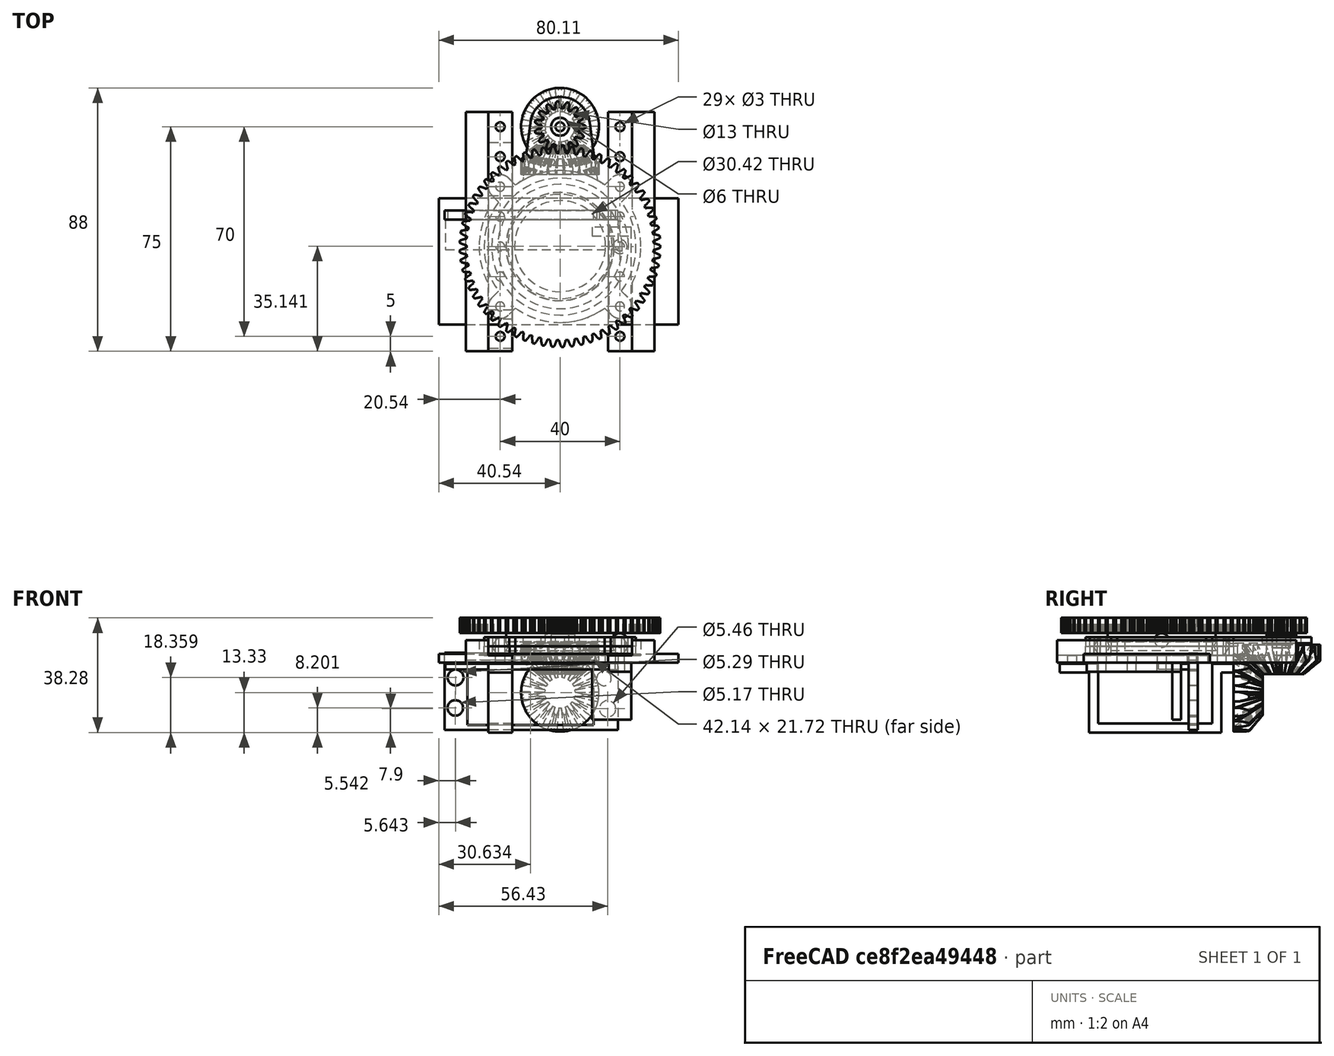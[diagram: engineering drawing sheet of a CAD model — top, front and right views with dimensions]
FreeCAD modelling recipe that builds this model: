
FCSTD DOCUMENT  (FreeCAD 0.16RUnknown)
Label: FrontTurntable2
License: CreativeCommons Attribution-NonCommercial
LicenseURL: http://creativecommons.org/licenses/by-nc/4.0/
objects: Sketcher::SketchObject×15, PartDesign::Pad×12, Part::Cylinder×5, Part::FeaturePython×4, Part::Feature×3, Part::MultiFuse×3, Part::Cut×3, Mesh::Feature×2, PartDesign::Revolution×2, Part::MultiCommon×1, Part::Sphere×1, Part::Mirroring×1
note: 64 computed .brp shape members not serialized (recipe doc carries the construction recipe); baked Part::Feature solids carry a one-line shape summary decoded from their .brp

FEATURE [Mesh::Feature] ParallaxServo
  Placement = pos=(-9.85,-60,0) rot=(-1,0,0;1.5708rad)
FEATURE [Part::FeaturePython] BevelGear  # WARN: FeaturePython — macro-defined, semantics opaque (R4)
  Placement = pos=(0,0,0) rot=(1,0,0;1.5708rad)
  backlash = 0
  clearance = 0.1
  height = 10
  m = 1.5
  numpoints = 6
  pitch_angle = 45
  pressure_angle = 20
  teeth = 15
FEATURE [Part::Cylinder] Cylinder
  Angle = 360
  Height = 10
  Placement = pos=(0,-6,0) rot=(1,0,0;1.5708rad)
  Radius = 13
FEATURE [Part::MultiCommon] Common
  Shapes = -> [BevelGear,Cylinder]
FEATURE [Part::Feature] Common001  label="Common"
  Placement = pos=(0,0,0) rot=(-1,0,0;1.5708rad)
  shape: bbox 39.21 x 39 x 10 mm, 93 faces (baked)
FEATURE [Sketcher::SketchObject] Sketch003
  Placement = pos=(0,-40,14) rot=(0.57735,0.57735,0.57735;2.0944rad)
  sketch-geometry (9):
    g0: LineSegment StartX=0 StartY=0 StartZ=0 EndX=18.1065 EndY=0 EndZ=0
    g1: LineSegment StartX=18.1065 StartY=3 StartZ=0 EndX=0 EndY=3 EndZ=0
    g2: LineSegment StartX=0 StartY=3 StartZ=0 EndX=0 EndY=0 EndZ=0
    g3: Circle [constr] CenterX=20 CenterY=1.5 CenterZ=0 NormalX=0 NormalY=0 NormalZ=1 Radius=2.25
    g4: LineSegment [constr] StartX=20 StartY=1.5 StartZ=0 EndX=0 EndY=1.5 EndZ=0
    g5: LineSegment StartX=18.1065 StartY=3 StartZ=0 EndX=17.4071 EndY=1.5 EndZ=0
    g6: LineSegment StartX=17.4071 StartY=1.5 StartZ=0 EndX=18.1065 EndY=0 EndZ=0
    g7: LineSegment [constr] StartX=18.1065 StartY=3 StartZ=0 EndX=18.1065 EndY=0 EndZ=0
    g8: Circle [constr] CenterX=20 CenterY=1.5 CenterZ=0 NormalX=0 NormalY=0 NormalZ=1 Radius=2.35
  constraints (23):
    c: Coincident(g-1,g0)
    c: PointOnObject(g1,g-2)
    c: Coincident(g1,g2)
    c: Coincident(g2,g0)
    c: PointOnObject(g0,g-1)
    c: Horizontal(g1)
    c: Radius(g3) = 2.25
    c: PointOnObject(g4,g2)
    c: Symmetric(g1,g-1,g4)
    c: DistanceY(g2,g2) = 3
    c: Coincident(g4,g3)
    c: Coincident(g5,g1)
    c: PointOnObject(g5,g4)
    c: Coincident(g6,g5)
    c: Coincident(g6,g0)
    c: Coincident(g7,g1)
    c: Coincident(g7,g0)
    c: Vertical(g7)
    c: Angle(g6,g5) = 2.26893
    c: Coincident(g8,g3)
    c: Radius(g8) = 2.35
    c: Tangent(g8,g5)
    c: DistanceX(g-1,g3) = 20
FEATURE [PartDesign::Revolution] Revolution
  Angle = 360
  Axis = (0,0,1)
  Base = (0,-40,14)
  Placement = pos=(0,-40,14) rot=(0.57735,0.57735,0.57735;2.0944rad)
  ReferenceAxis = -> Sketch003 [V_Axis]
  Reversed = true
  Sketch = -> Sketch003
FEATURE [Sketcher::SketchObject] Sketch004
  Placement = pos=(0,0,16) rot=(0.57735,0.57735,0.57735;2.0944rad)
  sketch-geometry (5):
    g0: Circle [constr] CenterX=20 CenterY=1.5 CenterZ=0 NormalX=0 NormalY=0 NormalZ=1 Radius=2.35
    g1: LineSegment StartX=20.7682 StartY=-1.5 StartZ=0 EndX=22.8688 EndY=1.5 EndZ=0
    g2: LineSegment StartX=22.8688 StartY=1.5 StartZ=0 EndX=25.3688 EndY=1.5 EndZ=0
    g3: LineSegment StartX=20.7682 StartY=-1.5 StartZ=0 EndX=25.3688 EndY=-1.5 EndZ=0
    g4: LineSegment StartX=25.3688 StartY=-1.5 StartZ=0 EndX=25.3688 EndY=1.5 EndZ=0
  constraints (15):
    c: Radius(g0) = 2.35
    c: DistanceX(g0) = 20
    c: DistanceY(g0) = 1.5
    c: Coincident(g1,g2)
    c: Horizontal(g2)
    c: Horizontal(g3)
    c: Coincident(g3,g4)
    c: Coincident(g4,g2)
    c: Vertical(g4)
    c: DistanceY(g-1,g2) = 1.5
    c: Tangent(g0,g1)
    c: DistanceX(g2,g2) = 2.5
    c: Coincident(g1,g3)
    c: Angle(g3,g1) = 0.959931
    c: DistanceY(g4,g4) = 3
FEATURE [PartDesign::Revolution] Revolution001
  Angle = 360
  Axis = (0,0,1)
  Base = (0,0,16)
  Placement = pos=(0,0,16) rot=(0.57735,0.57735,0.57735;2.0944rad)
  ReferenceAxis = -> Sketch004 [V_Axis]
  Reversed = true
  Sketch = -> Sketch004
FEATURE [Part::Sphere] Sphere
  Angle1 = -90
  Angle2 = 90
  Angle3 = 360
  Placement = pos=(20,-40,17.5) rot=(0,0,1;0rad)
  Radius = 2.35
FEATURE [Sketcher::SketchObject] Sketch005
  Placement = pos=(0,0,14.5) rot=(0,0,1;0rad)
  sketch-geometry (6):
    g0: Circle CenterX=20 CenterY=20 CenterZ=0 NormalX=0 NormalY=0 NormalZ=1 Radius=1.5
    g1: ArcOfCircle CenterX=0 CenterY=0 CenterZ=0 NormalX=0 NormalY=0 NormalZ=1 Radius=25 StartAngle=0.625164 EndAngle=0.945315
    g2: LineSegment [constr] StartX=20 StartY=20 StartZ=0 EndX=0 EndY=0 EndZ=0
    g3: ArcOfCircle CenterX=20 CenterY=20 CenterZ=0 NormalX=0 NormalY=0 NormalZ=1 Radius=4 StartAngle=5.42273 EndAngle=8.73713
    g4: LineSegment StartX=14.6372 StartY=20.267 StartZ=0 EndX=16.909 EndY=22.5389 EndZ=0
    g5: LineSegment StartX=20.2717 StartY=14.6308 StartZ=0 EndX=22.6084 EndY=16.9674 EndZ=0
  constraints (15):
    c: Radius(g0) = 1.5
    c: Coincident(g1,g-1)
    c: Radius(g1) = 25
    c: Coincident(g2,g0)
    c: Coincident(g2,g-1)
    c: Angle(g-1,g2) = 0.785398
    c: DistanceX(g-1,g0) = 20
    c: Coincident(g3,g0)
    c: Coincident(g4,g1)
    c: Coincident(g4,g3)
    c: Coincident(g5,g1)
    c: Coincident(g5,g3)
    c: Parallel(g5,g4)
    c: Parallel(g4,g2)
    c: Radius(g3) = 4
FEATURE [PartDesign::Pad] Pad  label="MountingJoint"
  Length = 3
  Length2 = 100
  Placement = pos=(0,0,14.5) rot=(0,0,1;0rad)
  Sketch = -> Sketch005
  Type = 0
FEATURE [Part::FeaturePython] Array  # Draft array (typed FeaturePython)
  Angle = 360
  ArrayType = 1
  Axis = (0,0,1)
  Base = -> Pad
  Center = (0,0,1)
  Fuse = false
  IntervalAxis = (0,0,0)
  IntervalX = (1,0,0)
  IntervalY = (0,1,0)
  IntervalZ = (0,0,0)
  NumberPolar = 4
  NumberX = 1
  NumberY = 1
  NumberZ = 1
FEATURE [Part::MultiFuse] Fusion
  Placement = pos=(0,-40,-2) rot=(0,0,1;0rad)
  Shapes = -> [Array,Revolution001]
FEATURE [Part::Feature] Fusion001  label="Fusion"
  Placement = pos=(0,-40,35) rot=(1,0,0;3.14159rad)
  shape: bbox 50.74 x 50.74 x 3 mm, 23 faces (baked)
FEATURE [Part::FeaturePython] InvoluteGear  # WARN: FeaturePython — macro-defined, semantics opaque (R4)
  Placement = pos=(0,0,20) rot=(0,0,1;0rad)
  backlash = 0
  beta = 0
  clearance = 0.25
  height = 5
  module = 1
  numpoints = 6
  pressure_angle = 20
  shift = 0
  simple = false
  teeth = 15
  undercut = false
FEATURE [Part::FeaturePython] InvoluteGear001  # WARN: FeaturePython — macro-defined, semantics opaque (R4)
  Placement = pos=(0,-40,20) rot=(0,0,1;0rad)
  backlash = 0
  beta = 0
  clearance = 0.25
  height = 5
  module = 1
  numpoints = 6
  pressure_angle = 20
  shift = 0
  simple = false
  teeth = 65
  undercut = false
FEATURE [Part::Cylinder] Cylinder001  label="Cylinder"
  Angle = 360
  Height = 10
  Placement = pos=(0,0,15) rot=(0,0,1;0rad)
  Radius = 3
FEATURE [Part::Cylinder] Cylinder002  label="Cylinder"
  Angle = 360
  Height = 3
  Placement = pos=(0,-40,17) rot=(0,0,1;0rad)
  Radius = 18
FEATURE [Sketcher::SketchObject] Sketch
  Placement = pos=(0,0,16.5) rot=(0,0,1;0rad)
  sketch-geometry (2):
    g0: Circle CenterX=0 CenterY=0 CenterZ=0 NormalX=0 NormalY=0 NormalZ=1 Radius=3
    g1: Circle CenterX=0 CenterY=0 CenterZ=0 NormalX=0 NormalY=0 NormalZ=1 Radius=5
  constraints (4):
    c: Coincident(g0,g-1)
    c: Radius(g0) = 3
    c: Coincident(g1,g-1)
    c: Radius(g1) = 5
FEATURE [PartDesign::Pad] Pad001  label="Bearing"
  Length = 3
  Length2 = 100
  Placement = pos=(0,0,16.5) rot=(0,0,1;0rad)
  Sketch = -> Sketch
  Type = 0
FEATURE [Part::Cylinder] Cylinder003  label="screw cutout"
  Angle = 360
  Height = 30
  Radius = 1.5
FEATURE [Part::Cylinder] Cylinder004  label="screw cutout"
  Angle = 360
  Height = 30
  Radius = 1.5
FEATURE [Part::Cut] Cut
  Base = -> Cylinder001
  Tool = -> Cylinder003
FEATURE [Part::Cut] Cut001
  Base = -> Common001
  Tool = -> Cylinder004
FEATURE [Sketcher::SketchObject] Sketch006
  Placement = pos=(0,0,10) rot=(0,0,1;0rad)
  sketch-geometry (5):
    g0: LineSegment StartX=-40.541 StartY=-66.0062 StartZ=0 EndX=39.5748 EndY=-66.0062 EndZ=0
    g1: LineSegment StartX=39.5748 StartY=-66.0062 StartZ=0 EndX=39.5748 EndY=-23.8558 EndZ=0
    g2: LineSegment StartX=39.5748 StartY=-23.8558 StartZ=0 EndX=-40.541 EndY=-23.8558 EndZ=0
    g3: LineSegment StartX=-40.541 StartY=-23.8558 StartZ=0 EndX=-40.541 EndY=-66.0062 EndZ=0
    g4: Circle CenterX=0 CenterY=-39.8595 CenterZ=0 NormalX=0 NormalY=0 NormalZ=1 Radius=15.2103
  constraints (9):
    c: Coincident(g0,g1)
    c: Coincident(g1,g2)
    c: Coincident(g2,g3)
    c: Coincident(g3,g0)
    c: Horizontal(g0)
    c: Horizontal(g2)
    c: Vertical(g1)
    c: Vertical(g3)
    c: PointOnObject(g4,g-2)
FEATURE [PartDesign::Pad] Pad002
  Length = 3
  Length2 = 100
  Placement = pos=(0,0,10) rot=(0,0,1;0rad)
  Sketch = -> Sketch006
  Type = 0
FEATURE [Sketcher::SketchObject] Sketch007
  Placement = pos=(0,-31,0) rot=(-1,0,0;4.71239rad)
  sketch-geometry (12):
    g0: LineSegment StartX=-38.5174 StartY=13.3252 StartZ=0 EndX=19.309 EndY=13.3252 EndZ=0
    g1: LineSegment StartX=19.309 StartY=13.3252 StartZ=0 EndX=19.309 EndY=-12.4201 EndZ=0
    g2: LineSegment StartX=19.309 StartY=-12.4201 StartZ=0 EndX=-38.5174 EndY=-12.4201 EndZ=0
    g3: LineSegment StartX=-38.5174 StartY=-12.4201 StartZ=0 EndX=-38.5174 EndY=13.3252 EndZ=0
    g4: LineSegment StartX=-30.9749 StartY=10.9116 StartZ=0 EndX=11.163 EndY=10.9116 EndZ=0
    g5: LineSegment StartX=11.163 StartY=10.9116 StartZ=0 EndX=11.163 EndY=-10.811 EndZ=0
    g6: LineSegment StartX=11.163 StartY=-10.811 StartZ=0 EndX=-30.9749 EndY=-10.811 EndZ=0
    g7: LineSegment StartX=-30.9749 StartY=-10.811 StartZ=0 EndX=-30.9749 EndY=10.9116 EndZ=0
    g8: Circle CenterX=14.6829 CenterY=4.77697 CenterZ=0 NormalX=0 NormalY=0 NormalZ=1 Radius=2.43241
    g9: Circle CenterX=15.8897 CenterY=-5.38037 CenterZ=0 NormalX=0 NormalY=0 NormalZ=1 Radius=2.73204
    g10: Circle CenterX=-34.897 CenterY=5.07867 CenterZ=0 NormalX=0 NormalY=0 NormalZ=1 Radius=2.64553
    g11: Circle CenterX=-34.9976 CenterY=-5.07867 CenterZ=0 NormalX=0 NormalY=0 NormalZ=1 Radius=2.58559
  constraints (16):
    c: Coincident(g0,g1)
    c: Coincident(g1,g2)
    c: Coincident(g2,g3)
    c: Coincident(g3,g0)
    c: Horizontal(g0)
    c: Horizontal(g2)
    c: Vertical(g1)
    c: Vertical(g3)
    c: Coincident(g4,g5)
    c: Coincident(g5,g6)
    c: Coincident(g6,g7)
    c: Coincident(g7,g4)
    c: Horizontal(g4)
    c: Horizontal(g6)
    c: Vertical(g5)
    c: Vertical(g7)
FEATURE [PartDesign::Pad] Pad003
  Length = 3
  Length2 = 100
  Placement = pos=(0,-31,0) rot=(-1,0,0;4.71239rad)
  Reversed = true
  Sketch = -> Sketch007
  Type = 0
FEATURE [Sketcher::SketchObject] Sketch008
  Placement = pos=(0,-31,0) rot=(1,0,0;1.5708rad)
  sketch-geometry (4):
    g0: LineSegment StartX=-38.2971 StartY=7.70587 StartZ=0 EndX=19.3119 EndY=7.70587 EndZ=0
    g1: LineSegment StartX=19.3119 StartY=7.70587 StartZ=0 EndX=19.3119 EndY=9.70587 EndZ=0
    g2: LineSegment StartX=19.3119 StartY=9.70587 StartZ=0 EndX=-38.2971 EndY=9.70587 EndZ=0
    g3: LineSegment StartX=-38.2971 StartY=9.70587 StartZ=0 EndX=-38.2971 EndY=7.70587 EndZ=0
  constraints (9):
    c: Coincident(g0,g1)
    c: Coincident(g1,g2)
    c: Coincident(g2,g3)
    c: Coincident(g3,g0)
    c: Horizontal(g0)
    c: Horizontal(g2)
    c: Vertical(g1)
    c: Vertical(g3)
    c: DistanceY(g1,g1) = 2
FEATURE [PartDesign::Pad] Pad004
  Length = 10
  Length2 = 100
  Placement = pos=(0,-31,0) rot=(1,0,0;1.5708rad)
  Sketch = -> Sketch008
  Type = 0
FEATURE [Sketcher::SketchObject] Sketch009
  Placement = pos=(0,0,18.5) rot=(0,0,1;0rad)
  sketch-geometry (5):
    g0: Circle CenterX=0 CenterY=0 CenterZ=0 NormalX=0 NormalY=0 NormalZ=1 Radius=6.5
    g1: ArcOfCircle CenterX=0 CenterY=0 CenterZ=0 NormalX=0 NormalY=0 NormalZ=1 Radius=10 StartAngle=0.130798 EndAngle=3.01079
    g2: LineSegment StartX=-9.91458 StartY=1.30426 StartZ=0 EndX=-12.5 EndY=-18.3494 EndZ=0
    g3: LineSegment StartX=9.91458 StartY=1.30426 StartZ=0 EndX=12.5 EndY=-18.3494 EndZ=0
    g4: ArcOfCircle CenterX=0 CenterY=-40 CenterZ=0 NormalX=0 NormalY=0 NormalZ=1 Radius=25 StartAngle=1.0472 EndAngle=2.0944
  constraints (13):
    c: Coincident(g0,g-1)
    c: Radius(g0) = 6.5
    c: Coincident(g1,g-1)
    c: Tangent(g1,g2) = -1.5708
    c: Tangent(g1,g3) = 1.5708
    c: PointOnObject(g4,g-2)
    c: Coincident(g4,g2)
    c: Coincident(g4,g3)
    c: Radius(g4) = 25
    c: DistanceY(g4,g-1) = 40
    c: Symmetric(g2,g3,g-2)
    c: Radius(g1) = 10
    c: DistanceX(g2,g3) = 25
FEATURE [PartDesign::Pad] Pad005
  Length = 2
  Length2 = 100
  Placement = pos=(0,0,18.5) rot=(0,0,1;0rad)
  Sketch = -> Sketch009
  Type = 0
FEATURE [Part::MultiFuse] Fusion002
  Placement = pos=(0,0,-2) rot=(0,0,1;0rad)
  Shapes = -> [Fusion001,Pad005]
FEATURE [Sketcher::SketchObject] Sketch010
  Placement = pos=(0,0,10) rot=(0,0,1;0rad)
  sketch-geometry (4):
    g0: LineSegment StartX=0 StartY=-80 StartZ=0 EndX=7.5 EndY=-80 EndZ=0
    g1: LineSegment StartX=7.5 StartY=-80 StartZ=0 EndX=7.5 EndY=0 EndZ=0
    g2: LineSegment StartX=7.5 StartY=0 StartZ=0 EndX=0 EndY=0 EndZ=0
    g3: LineSegment StartX=0 StartY=0 StartZ=0 EndX=0 EndY=-80 EndZ=0
  constraints (11):
    c: Coincident(g0,g1)
    c: Coincident(g1,g2)
    c: Coincident(g2,g3)
    c: Coincident(g3,g0)
    c: Horizontal(g0)
    c: Horizontal(g2)
    c: Vertical(g1)
    c: Vertical(g3)
    c: DistanceY(g1,g1) = 80
    c: DistanceX(g2,g2) = 7.5
    c: Coincident(g-1,g2)
FEATURE [PartDesign::Pad] Pad006
  Length = 7.5
  Length2 = 100
  Placement = pos=(0,0,10) rot=(0,0,1;0rad)
  Sketch = -> Sketch010
  Type = 0
FEATURE [Sketcher::SketchObject] Sketch011
  Placement = pos=(0,0,10) rot=(0,0,1;0rad)
  sketch-geometry (19):
    g0: LineSegment StartX=0 StartY=0 StartZ=0 EndX=0 EndY=-80 EndZ=0
    g1: Circle CenterX=-4 CenterY=-45 CenterZ=0 NormalX=0 NormalY=0 NormalZ=1 Radius=1.5
    g2: Circle CenterX=-4 CenterY=-65 CenterZ=0 NormalX=0 NormalY=0 NormalZ=1 Radius=1.5
    g3: Circle CenterX=-4 CenterY=-55 CenterZ=0 NormalX=0 NormalY=0 NormalZ=1 Radius=1.5
    g4: Circle CenterX=-4 CenterY=-75 CenterZ=0 NormalX=0 NormalY=0 NormalZ=1 Radius=1.5
    g5: LineSegment [constr] StartX=-4 StartY=-45 StartZ=0 EndX=-4 EndY=-55 EndZ=0
    g6: LineSegment [constr] StartX=-4 StartY=-55 StartZ=0 EndX=-4 EndY=-65 EndZ=0
    g7: LineSegment [constr] StartX=-4 StartY=-65 StartZ=0 EndX=-4 EndY=-75 EndZ=0
    g8: Circle CenterX=-4 CenterY=-35 CenterZ=0 NormalX=0 NormalY=0 NormalZ=1 Radius=1.5
    g9: Circle CenterX=-4 CenterY=-25 CenterZ=0 NormalX=0 NormalY=0 NormalZ=1 Radius=1.5
    g10: Circle CenterX=-4 CenterY=-15 CenterZ=0 NormalX=0 NormalY=0 NormalZ=1 Radius=1.5
    g11: LineSegment [constr] StartX=-4 StartY=-45 StartZ=0 EndX=-4 EndY=-35 EndZ=0
    g12: LineSegment [constr] StartX=-4 StartY=-35 StartZ=0 EndX=-4 EndY=-25 EndZ=0
    g13: LineSegment [constr] StartX=-4 StartY=-25 StartZ=0 EndX=-4 EndY=-15 EndZ=0
    g14: Circle CenterX=-4 CenterY=-5 CenterZ=0 NormalX=0 NormalY=0 NormalZ=1 Radius=1.5
    g15: LineSegment [constr] StartX=-4 StartY=-5 StartZ=0 EndX=-4 EndY=-15 EndZ=0
    g16: LineSegment StartX=0 StartY=0 StartZ=0 EndX=-8 EndY=0 EndZ=0
    g17: LineSegment StartX=-8 StartY=0 StartZ=0 EndX=-8 EndY=-80 EndZ=0
    g18: LineSegment StartX=-8 StartY=-80 StartZ=0 EndX=0 EndY=-80 EndZ=0
  constraints (49):
    c: Coincident(g0,g-1)
    c: Vertical(g0)
    c: DistanceY(g0,g0) = 80
    c: Coincident(g5,g1)
    c: Coincident(g5,g3)
    c: Coincident(g5,g6)
    c: Coincident(g6,g2)
    c: Coincident(g6,g7)
    c: Coincident(g7,g4)
    c: Vertical(g7)
    c: Vertical(g6)
    c: Vertical(g5)
    c: Equal(g5,g6)
    c: Equal(g6,g7)
    c: DistanceY(g5,g5) = 10
    c: Coincident(g11,g1)
    c: Coincident(g11,g8)
    c: Vertical(g11)
    c: Coincident(g11,g12)
    c: Coincident(g12,g9)
    c: Coincident(g12,g13)
    c: Coincident(g13,g10)
    c: Vertical(g12)
    c: Vertical(g13)
    c: Equal(g13,g12)
    c: Equal(g12,g11)
    c: Equal(g3,g2)
    c: Equal(g2,g1)
    c: Equal(g1,g8)
    c: Equal(g8,g9)
    c: Equal(g9,g10)
    c: Equal(g10,g4)
    c: DistanceY(g0,g4) = 5
    c: Equal(g11,g5)
    c: Coincident(g15,g14)
    c: Coincident(g15,g10)
    c: Vertical(g15)
    c: Equal(g15,g13)
    c: Equal(g14,g10)
    c: Radius(g14) = 1.5
    c: DistanceX(g14,g-1) = 4
    c: Coincident(g-1,g16)
    c: Coincident(g16,g17)
    c: Coincident(g17,g18)
    c: Coincident(g18,g0)
    c: Vertical(g17)
    c: Horizontal(g18)
    c: DistanceX(g18,g18) = 8
    c: Horizontal(g16)
FEATURE [PartDesign::Pad] Pad007
  Length = 2.5
  Length2 = 100
  Placement = pos=(0,0,10) rot=(0,0,1;0rad)
  Sketch = -> Sketch011
  Type = 0
FEATURE [Part::MultiFuse] Fusion003
  Placement = pos=(24,5,0) rot=(0,0,1;0rad)
  Shapes = -> [Pad006,Pad007]
FEATURE [Sketcher::SketchObject] Sketch012
FEATURE [Sketcher::SketchObject] Sketch013
  Placement = pos=(0,-40,12.5) rot=(0,0,1;0rad)
  sketch-geometry (1):
    g0: Circle CenterX=0 CenterY=0 CenterZ=0 NormalX=0 NormalY=0 NormalZ=1 Radius=27
  constraints (2):
    c: Coincident(g0,g-1)
    c: Radius(g0) = 27
FEATURE [PartDesign::Pad] Pad008
  Length = 10
  Length2 = 100
  Placement = pos=(0,-40,12.5) rot=(0,0,1;0rad)
  Sketch = -> Sketch013
  Type = 0
FEATURE [Part::Cut] Cut002
  Base = -> Fusion003
  Tool = -> Pad008
FEATURE [Part::Feature] Cut002001  label="Cut002"
  Placement = pos=(0,0,2) rot=(0,0,1;0rad)
  shape: bbox 15.5 x 80 x 7.5 mm, 18 faces (baked)
FEATURE [Part::Mirroring] Part__Mirroring  label="Cut002 (Mirror #1)"
  Base = (0,0,0)
  Normal = (1,0,0)
  Placement = pos=(0,0,-2) rot=(0,0,1;0rad)
  Source = -> Cut002001
FEATURE [Mesh::Feature] ParallaxServo001
  Placement = pos=(0,13,-23) rot=(0,0,-1;1.5708rad)
FEATURE [Sketcher::SketchObject] Sketch014
  Placement = pos=(-16,0,0) rot=(0.57735,0.57735,0.57735;2.0944rad)
  sketch-geometry (15):
    g0: LineSegment StartX=-74.0927 StartY=9.72407 StartZ=0 EndX=-61.2689 EndY=9.72407 EndZ=0
    g1: LineSegment StartX=-61.2689 StartY=9.72407 StartZ=0 EndX=-61.2689 EndY=-10.2759 EndZ=0
    g2: LineSegment StartX=-61.2689 StartY=-10.2759 StartZ=0 EndX=-23.1313 EndY=-10.2759 EndZ=0
    g3: LineSegment StartX=-23.1313 StartY=-10.2759 StartZ=0 EndX=-23.1313 EndY=9.72407 EndZ=0
    g4: LineSegment StartX=-23.1313 StartY=9.72407 StartZ=0 EndX=-5.32485 EndY=9.72407 EndZ=0
    g5: LineSegment StartX=-5.32485 StartY=9.72407 StartZ=0 EndX=-5.32485 EndY=6.72407 EndZ=0
    g6: LineSegment StartX=-5.32485 StartY=6.72407 StartZ=0 EndX=-20.1313 EndY=6.72407 EndZ=0
    g7: LineSegment StartX=-20.1313 StartY=6.72407 StartZ=0 EndX=-20.1313 EndY=-13.2759 EndZ=0
    g8: LineSegment StartX=-20.1313 StartY=-13.2759 StartZ=0 EndX=-64.2689 EndY=-13.2759 EndZ=0
    g9: LineSegment StartX=-64.2689 StartY=-13.2759 StartZ=0 EndX=-64.2689 EndY=6.72407 EndZ=0
    g10: LineSegment StartX=-64.2689 StartY=6.72407 StartZ=0 EndX=-74.0927 EndY=6.72407 EndZ=0
    g11: LineSegment StartX=-74.0927 StartY=6.72407 StartZ=0 EndX=-74.0927 EndY=9.72407 EndZ=0
    g12: LineSegment [constr] StartX=-61.2689 StartY=-10.2759 StartZ=0 EndX=-64.2689 EndY=-10.2759 EndZ=0
    g13: LineSegment [constr] StartX=-61.2689 StartY=-10.2759 StartZ=0 EndX=-61.2689 EndY=-13.2759 EndZ=0
    g14: LineSegment [constr] StartX=-23.1313 StartY=-10.2759 StartZ=0 EndX=-20.1313 EndY=-10.2759 EndZ=0
  constraints (41):
    c: Horizontal(g0)
    c: Coincident(g0,g1)
    c: Vertical(g1)
    c: Coincident(g1,g2)
    c: Horizontal(g2)
    c: Coincident(g2,g3)
    c: Vertical(g3)
    c: Coincident(g3,g4)
    c: Horizontal(g4)
    c: Coincident(g4,g5)
    c: Vertical(g5)
    c: Coincident(g5,g6)
    c: Horizontal(g6)
    c: Coincident(g6,g7)
    c: Vertical(g7)
    c: Coincident(g7,g8)
    c: Horizontal(g8)
    c: Coincident(g8,g9)
    c: Vertical(g9)
    c: Coincident(g9,g10)
    c: Horizontal(g10)
    c: Coincident(g10,g11)
    c: Coincident(g11,g0)
    c: Vertical(g11)
    c: Equal(g11,g5)
    c: Coincident(g12,g1)
    c: PointOnObject(g12,g9)
    c: Horizontal(g12)
    c: Coincident(g13,g1)
    c: PointOnObject(g13,g8)
    c: Vertical(g13)
    c: Coincident(g14,g2)
    c: PointOnObject(g14,g7)
    c: Horizontal(g14)
    c: Equal(g12,g13)
    c: Equal(g13,g14)
    c: Equal(g14,g5)
    c: DistanceY(g11,g11) = 3
    c: DistanceX(g2,g2) = 38.1376
    c: DistanceY(g1,g1) = 20
    c: Equal(g1,g3)
FEATURE [PartDesign::Pad] Pad009
  Length = 8
  Length2 = 100
  Placement = pos=(-16,0,0) rot=(0.57735,0.57735,0.57735;2.0944rad)
  Reversed = true
  Sketch = -> Sketch014
  Type = 0
FEATURE [Sketcher::SketchObject] Sketch015
  Placement = pos=(20,-40,10) rot=(0,0,1;0rad)
  sketch-geometry (7):
    g0: LineSegment StartX=3.75 StartY=-25 StartZ=0 EndX=3.75 EndY=6.5 EndZ=0
    g1: LineSegment StartX=3.75 StartY=6.5 StartZ=0 EndX=-3.75 EndY=6.5 EndZ=0
    g2: LineSegment StartX=-3.75 StartY=6.5 StartZ=0 EndX=-3.75 EndY=-25 EndZ=0
    g3: LineSegment StartX=-3.75 StartY=-25 StartZ=0 EndX=3.75 EndY=-25 EndZ=0
    g4: Circle CenterX=0 CenterY=0 CenterZ=0 NormalX=0 NormalY=0 NormalZ=1 Radius=1.5
    g5: Circle CenterX=0 CenterY=-10 CenterZ=0 NormalX=0 NormalY=0 NormalZ=1 Radius=1.5
    g6: Circle CenterX=0 CenterY=-20 CenterZ=0 NormalX=0 NormalY=0 NormalZ=1 Radius=1.5
  constraints (20):
    c: Vertical(g0)
    c: Coincident(g0,g1)
    c: Vertical(g2)
    c: Coincident(g2,g3)
    c: Coincident(g3,g0)
    c: Horizontal(g3)
    c: DistanceX(g3,g3) = 7.5
    c: Coincident(g1,g2)
    c: PointOnObject(g4,g-2)
    c: PointOnObject(g5,g-2)
    c: PointOnObject(g6,g-2)
    c: Symmetric(g1,g0,g-2)
    c: DistanceY(g5,g4) = 10
    c: DistanceY(g6,g5) = 10
    c: DistanceY(g0,g6) = 5
    c: Radius(g4) = 1.5
    c: Equal(g4,g5)
    c: Equal(g4,g6)
    c: Coincident(g4,g-1)
    c: DistanceY(g-1,g1) = 6.5
FEATURE [Sketcher::SketchObject] Sketch016
  Placement = pos=(20,-40,10) rot=(0,0,1;0rad)
  sketch-geometry (4):
    g0: LineSegment StartX=3.75 StartY=6.5 StartZ=0 EndX=-9.25 EndY=6.5 EndZ=0
    g1: LineSegment StartX=-9.25 StartY=6.5 StartZ=0 EndX=-9.25 EndY=3.5 EndZ=0
    g2: LineSegment StartX=-9.25 StartY=3.5 StartZ=0 EndX=3.75 EndY=3.5 EndZ=0
    g3: LineSegment StartX=3.75 StartY=3.5 StartZ=0 EndX=3.75 EndY=6.5 EndZ=0
  constraints (12):
    c: Coincident(g0,g1)
    c: Coincident(g1,g2)
    c: Coincident(g2,g3)
    c: Coincident(g3,g0)
    c: Horizontal(g0)
    c: Horizontal(g2)
    c: Vertical(g1)
    c: Vertical(g3)
    c: DistanceY(g-1,g0) = 6.5
    c: DistanceX(g0,g0) = 13
    c: DistanceX(g-1,g2) = 3.75
    c: DistanceY(g1,g1) = 3
FEATURE [PartDesign::Pad] Pad010
  Length = 3
  Length2 = 100
  Placement = pos=(20,-40,10) rot=(0,0,1;0rad)
  Reversed = true
  Sketch = -> Sketch015
  Type = 0
FEATURE [PartDesign::Pad] Pad011
  Length = 19
  Length2 = 100
  Placement = pos=(20,-40,10) rot=(0,0,1;0rad)
  Reversed = true
  Sketch = -> Sketch016
  Type = 0
